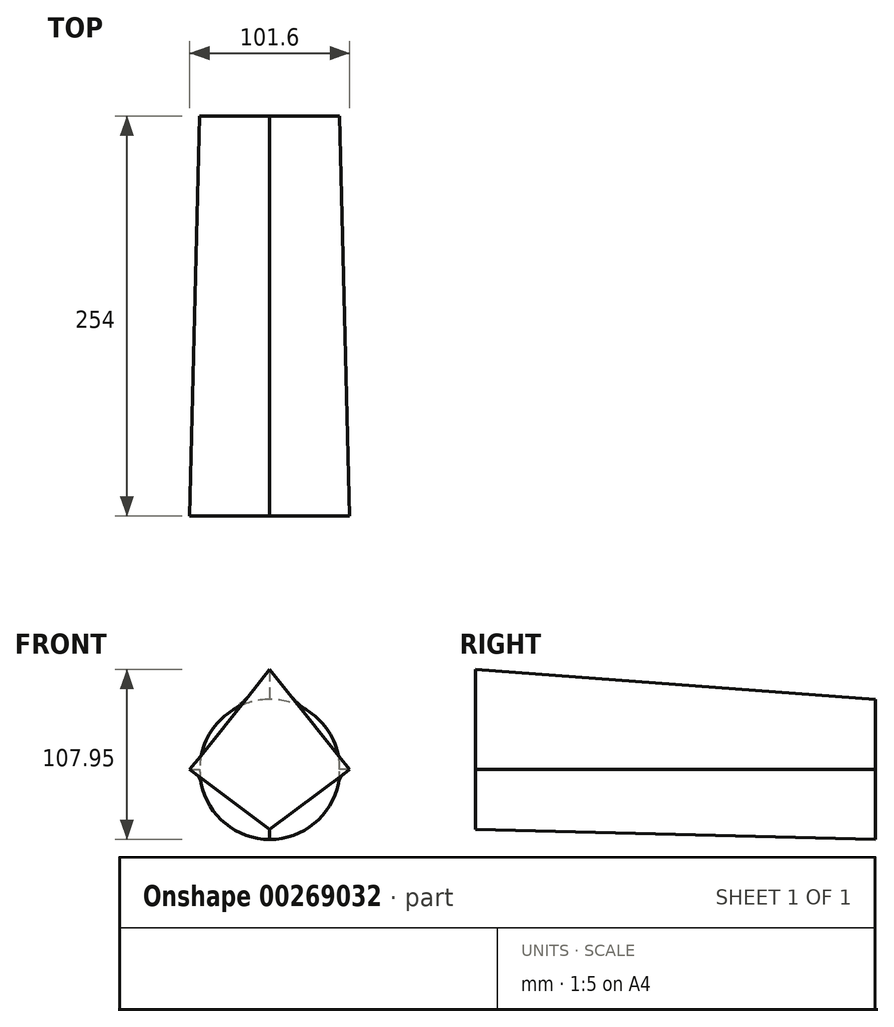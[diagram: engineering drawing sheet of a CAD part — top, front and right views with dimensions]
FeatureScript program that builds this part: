
annotation { "Feature Type Name" : "Feature", "Feature Type Description" : "" }
export const myFeature = defineFeature(function(context is Context, id is Id, definition is map)
    precondition{}
    {
        {
            var Q0;
            Q0=qCreatedBy(makeId("Front.planeOp"),FACE);
            cPlane(context, id + "F0", {"entities" : qUnion([Q0]), "cplaneType" : CPlaneType.OFFSET, "offset" : 254 * mm, "oppositeDirection" : true, "width" : 152.4 * mm, "height" : 152.4 * mm});
        }
        {
            var Q0;
            Q0=qCreatedBy(makeId("Front.planeOp"),FACE);
            var sketch = newSketch(context, id + "F1", { "sketchPlane" : qUnion([Q0])});
            skLineSegment(sketch, "E0", {"start": v(0, 63.5) * mm, "end": v(-50.8, 0) * mm});
            skLineSegment(sketch, "E1", {"start": v(-50.8, 0) * mm, "end": v(0, -38.1) * mm});
            skLineSegment(sketch, "E2", {"start": v(0, -38.1) * mm, "end": v(50.8, 0) * mm});
            skLineSegment(sketch, "E3", {"start": v(50.8, 0) * mm, "end": v(0, 63.5) * mm});
            skSolve(sketch);
        }
        {
            var Q0;
            Q0=qCreatedBy(id+"F0.planeOp",FACE);
            var sketch = newSketch(context, id + "F2", { "sketchPlane" : qUnion([Q0])});
            skCircle(sketch, "E4", {"center": v(0, 0) * mm, "radius": 44.45 * mm});
            skSolve(sketch);
        }
        {
            var Q0;
            Q0=makeQuery(id+"F1.imprint","IMPRINT",FACE,{"disambiguationData":[TD([[makeQuery(id+"F1.imprint","IMPRINT",EDGE,{"derivedFrom":sQuery(id+"F1.wireOp",EDGE,"E0")}),1.0]])]});
            var Q1;
            Q1=makeQuery(id+"F2.imprint","IMPRINT",FACE,{"disambiguationData":[TD([[makeQuery(id+"F2.imprint","IMPRINT",EDGE,{"derivedFrom":sQuery(id+"F2.wireOp",EDGE,"E4")}),1.0]])]});
            loft(context, id + "F3", {"sheetProfilesArray" : [{ "sheetProfileEntities" : qUnion([Q0]) }, { "sheetProfileEntities" : qUnion([Q1]) }]});
        }
    });
